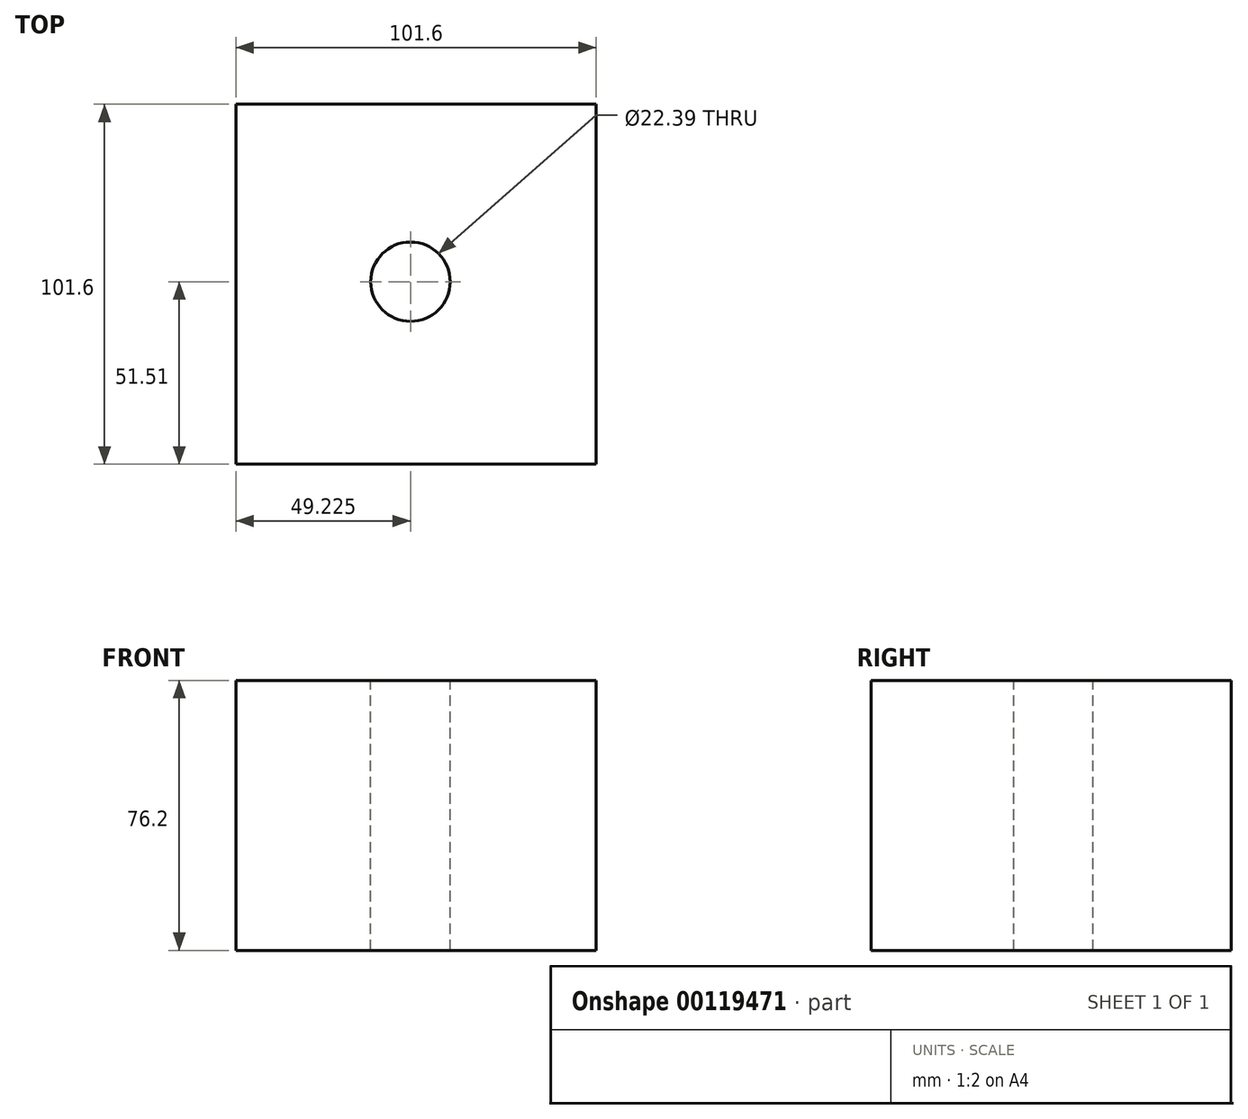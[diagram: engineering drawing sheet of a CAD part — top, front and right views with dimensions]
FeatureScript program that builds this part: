
annotation { "Feature Type Name" : "Feature", "Feature Type Description" : "" }
export const myFeature = defineFeature(function(context is Context, id is Id, definition is map)
    precondition{}
    {
        {
            var Q0;
            Q0=qCreatedBy(makeId("Top.planeOp"),FACE);
            var sketch = newSketch(context, id + "F0", { "sketchPlane" : qUnion([Q0])});
            skLineSegment(sketch, "E0.bottom", {"start": v(49.09, -47.26) * mm, "end": v(-52.51, -47.26) * mm});
            skLineSegment(sketch, "E0.top", {"start": v(49.09, 54.34) * mm, "end": v(-52.51, 54.34) * mm});
            skLineSegment(sketch, "E0.left", {"start": v(49.09, -47.26) * mm, "end": v(49.09, 54.34) * mm});
            skLineSegment(sketch, "E0.right", {"start": v(-52.51, -47.26) * mm, "end": v(-52.51, 54.34) * mm});
            skPoint(sketch, "E0.middle", {"position": v(-1.71, 3.54) * mm});
            skSolve(sketch);
        }
        {
            var Q0;
            Q0=makeQuery(id+"F0.imprint","IMPRINT",FACE,{"disambiguationData":[TD([[makeQuery(id+"F0.imprint","IMPRINT",EDGE,{"derivedFrom":sQuery(id+"F0.wireOp",EDGE,"E0.bottom")}),-1.0]])]});
            extrude(context, id + "F1", {"entities" : qUnion([Q0]), "depth" : 76.2 * mm});
        }
        {
            var Q0;
            Q0=makeQuery(id+"F1.opExtrude","CAP_FACE",FACE,{"disambiguationData":[OSD([sQuery(id+"F0.wireOp",EDGE,"E0.bottom"),sQuery(id+"F0.wireOp",EDGE,"E0.top"),sQuery(id+"F0.wireOp",EDGE,"E0.left"),sQuery(id+"F0.wireOp",EDGE,"E0.right")])],"isStart":false});
            var sketch = newSketch(context, id + "F2", { "sketchPlane" : qUnion([Q0])});
            skCircle(sketch, "E1", {"center": v(-3.28, 4.25) * mm, "radius": 11.2 * mm});
            skSolve(sketch);
        }
        {
            var Q0;
            Q0=makeQuery(id+"F1.opExtrude","SWEPT_FACE",FACE,{"disambiguationData":[OSD([sQuery(id+"F0.wireOp",EDGE,"E0.left")])]});
            var sketch = newSketch(context, id + "F3", { "sketchPlane" : qUnion([Q0])});
            skText(sketch, "E2", { "text": "A", "fontName": "OpenSans-Regular.ttf"});
            const initialGuessF3  = {"E2": [-0.01215, 0.02742, 1, 0, 0.01126]};
            skSetInitialGuess(sketch, initialGuessF3);
            skSolve(sketch);
        }
        {
            var Q0;
            Q0=makeQuery(id+"F3.imprint","IMPRINT",FACE,{"disambiguationData":[TD([[makeQuery(id+"F3.imprint","IMPRINT",EDGE,{"derivedFrom":sQuery(id+"F3.wireOp",EDGE,"E2.sketch_text.stroke-0")}),-1.0]])]});
            var Q1;
            Q1=makeQuery(id+"F3.imprint","IMPRINT",FACE,{"disambiguationData":[TD([[makeQuery(id+"F3.imprint","IMPRINT",EDGE,{"derivedFrom":sQuery(id+"F3.wireOp",EDGE,"E2.sketch_text.stroke-0")}),1.0]])]});
            extrude(context, id + "F4", {"entities" : qUnion([Q0, Q1]), "operationType" : NewBodyOperationType.ADD, "oppositeDirection" : true, "depth" : 19.05 * mm});
        }
        {
            var Q0;
            Q0=makeQuery(id+"F1.opExtrude","SWEPT_FACE",FACE,{"disambiguationData":[OSD([sQuery(id+"F0.wireOp",EDGE,"E0.bottom")])]});
            var sketch = newSketch(context, id + "F5", { "sketchPlane" : qUnion([Q0])});
            skText(sketch, "E3", { "text": "E", "fontName": "OpenSans-Regular.ttf"});
            const initialGuessF5  = {"E3": [-0.00468, 0.04249, 1, 0, 0.02558]};
            skSetInitialGuess(sketch, initialGuessF5);
            skSolve(sketch);
        }
        {
            var Q0;
            Q0=makeQuery(id+"F5.imprint","IMPRINT",FACE,{"disambiguationData":[TD([[makeQuery(id+"F5.imprint","IMPRINT",EDGE,{"derivedFrom":sQuery(id+"F5.wireOp",EDGE,"E3.sketch_text.stroke-0")}),-1.0]])]});
            extrude(context, id + "F6", {"entities" : qUnion([Q0]), "operationType" : NewBodyOperationType.ADD, "oppositeDirection" : true, "depth" : 76.2 * mm});
        }
        {
            var Q0;
            Q0=makeQuery(id+"F2.imprint","IMPRINT",FACE,{"disambiguationData":[TD([[makeQuery(id+"F2.imprint","IMPRINT",EDGE,{"derivedFrom":sQuery(id+"F2.wireOp",EDGE,"E1")}),1.0]])]});
            var Q1;
            Q1=sQuery(id+"F2.wireOp",EDGE,"E1");
            extrude(context, id + "F7", {"entities" : qUnion([Q0]), "operationType" : NewBodyOperationType.REMOVE, "surfaceEntities" : qUnion([Q1]), "oppositeDirection" : true, "depth" : 190.5 * mm});
        }
    });
